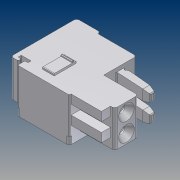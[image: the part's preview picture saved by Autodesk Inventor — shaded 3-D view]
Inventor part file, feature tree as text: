
AUTODESK INVENTOR PART (.ipt)
format: ipt  version: 2012 (Build 160160000, 160)  size: 337,408 bytes
history: native  units: mm (DEFAULTED — no unit token found)
features: sketch x20, extrude x19, pattern_linear x6, revolve x1
ambient origin geometry x8: Origin, YZ Plane, XZ Plane, XY Plane, X Axis, Y Axis, Z Axis, Center Point
bodies: Solid1 (feature_tree)
feature tree (46):
  extrude  "Extrusion1"  Depth=1.5mm TaperAngle=0.0deg
  extrude  "Extrusion2"  Depth=1.5mm TaperAngle=0.0deg
  extrude  "Extrusion3"  Depth=1.5mm TaperAngle=0.0deg
  extrude  "Extrusion4"  Depth=1.5mm TaperAngle=0.0deg
  extrude  "Extrusion5"  TaperAngle=360.0deg  [1 undecoded]
  extrude  "Extrusion6"  Depth=3.3mm TaperAngle=0.0deg
  extrude  "Extrusion7"  Depth=1.0mm TaperAngle=0.0deg
  extrude  "Extrusion8"  Depth=1.0mm TaperAngle=0.0deg
  extrude  "Extrusion9"  Depth=0.9mm TaperAngle=0.0deg
  revolve  "Revolution1"  [1 undecoded]
  pattern_linear  "Rectangular Pattern1"  Count1=2 Spacing1=3.5mm
  extrude  "Extrusion10"  Depth=20.0mm TaperAngle=0.0deg
  pattern_linear  "Rectangular Pattern2"  [2 undecoded]
  extrude  "Extrusion11"  [1 undecoded]
  pattern_linear  "Rectangular Pattern3"  [2 undecoded]
  extrude  "Extrusion12"  [1 undecoded]
  pattern_linear  "Rectangular Pattern4"  [2 undecoded]
  extrude  "Extrusion13"  [1 undecoded]
  extrude  "Extrusion14"  [1 undecoded]
  extrude  "Extrusion15"  [1 undecoded]
  extrude  "Extrusion16"  [1 undecoded]
  extrude  "Extrusion17"  [1 undecoded]
  pattern_linear  "Rectangular Pattern5"  [2 undecoded]
  extrude  "Extrusion18"  [1 undecoded]
  pattern_linear  "Rectangular Pattern6"  [2 undecoded]
  extrude  "Extrusion19"  [1 undecoded]
  sketch  "Skizze_1"  dims[d0=7.0mm d1=0.0mm d2=1.5mm d3=0.0mm]
  sketch  "Skizze_3"  dims[d8=1.5mm d9=0.0mm d10=1.5mm d11=0.0mm]
  sketch  "Skizze_4"  dims[d12=1.5mm d13=0.0mm d14=1.5mm d15=0.0mm]
  sketch  "Skizze_5"  dims[d16=1.4mm d17=0.0mm d18=360.0deg]
  sketch  "Skizze_6"  dims[d19=20.0mm d21=3.5mm d22=10.0mm d24=0.0mm d25=3.3mm d26=0.0mm]
  sketch  "Skizze_7"  dims[d27=20.0mm d29=3.5mm d30=10.0mm d32=0.0mm d33=1.0mm d34=0.0mm]
  sketch  "Skizze_8"  dims[d35=20.0mm d37=3.5mm d38=10.0mm d40=0.0mm d41=1.0mm d42=0.0mm]
  sketch  "Skizze_9"  dims[d43=20.0mm d45=3.5mm d46=10.0mm d48=0.0mm d49=0.9mm d50=0.0mm]
  sketch  "Skizze_2"  dims[d4=1.5mm d5=0.0mm d6=1.5mm d7=0.0mm]
  sketch  "Skizze_10"  dims[d51=0.9mm d52=0.0mm d53=1.7mm d54=0.0mm]
  sketch  "Skizze_12"  dims[d55=1.7mm d56=0.0mm]
  sketch  "Skizze_14"  dims[d57=2.0mm d58=0.0mm d59=20.0mm d61=3.5mm d62=10.0mm d64=0.0mm]
  sketch  "Skizze_16"  dims[d65=1.7mm d66=0.0mm d67=20.0mm d69=3.5mm d70=10.0mm d72=0.0mm]
  sketch  "Skizze_18"  dims[d73=2.2mm d74=0.0mm]
  sketch  "Skizze_19"
  sketch  "Skizze_20"
  sketch  "Skizze_21"
  sketch  "Skizze_22"
  sketch  "Skizze_24"
  sketch  "Skizze_26"
note: 21 required parameter values undecoded (feature->parameter linkage not recoverable at this tier; creation-order binding heuristic only, values carry confidence <= 0.55)